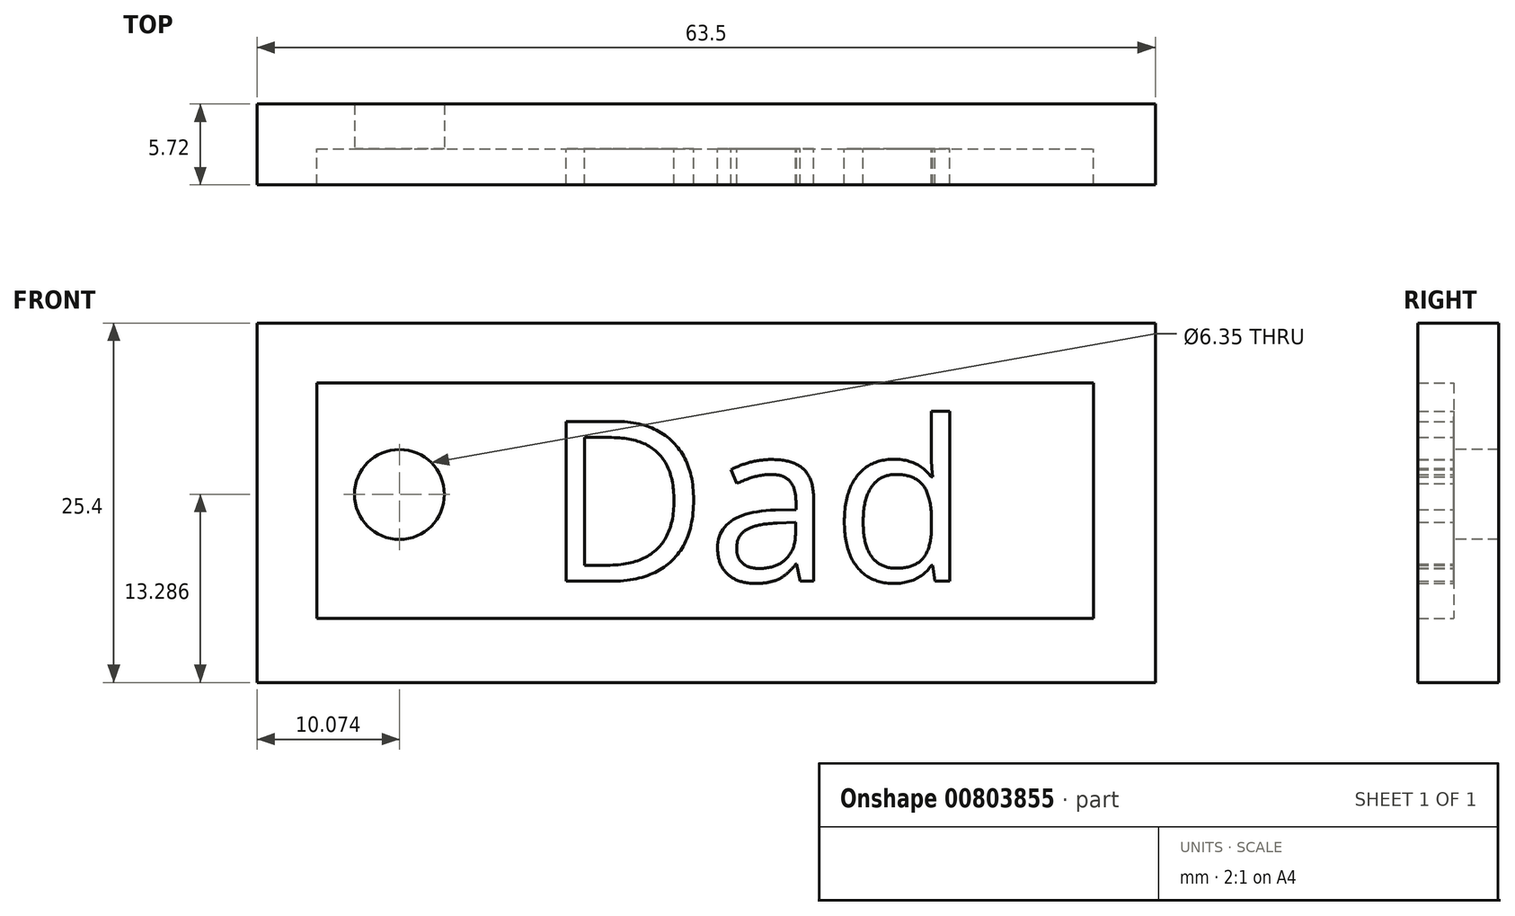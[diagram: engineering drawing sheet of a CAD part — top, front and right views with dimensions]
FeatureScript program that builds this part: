
annotation { "Feature Type Name" : "Feature", "Feature Type Description" : "" }
export const myFeature = defineFeature(function(context is Context, id is Id, definition is map)
    precondition{}
    {
        {
            var Q0;
            Q0=qCreatedBy(makeId("Front.planeOp"),FACE);
            var sketch = newSketch(context, id + "F0", { "sketchPlane" : qUnion([Q0])});
            skLineSegment(sketch, "E0.bottom", {"start": v(0, 0) * mm, "end": v(63.5, 0) * mm});
            skLineSegment(sketch, "E0.top", {"start": v(0, 25.4) * mm, "end": v(63.5, 25.4) * mm});
            skLineSegment(sketch, "E0.left", {"start": v(0, 0) * mm, "end": v(0, 25.4) * mm});
            skLineSegment(sketch, "E0.right", {"start": v(63.5, 0) * mm, "end": v(63.5, 25.4) * mm});
            skSolve(sketch);
        }
        {
            var Q0;
            Q0=makeQuery(id+"F0.imprint","IMPRINT",FACE,{"disambiguationData":[TD([[makeQuery(id+"F0.imprint","IMPRINT",EDGE,{"derivedFrom":sQuery(id+"F0.wireOp",EDGE,"E0.bottom")}),1.0]])]});
            extrude(context, id + "F1", {"entities" : qUnion([Q0]), "depth" : 3.17 * mm, "offsetDistance" : 25.4 * mm});
        }
        {
            var Q0;
            Q0=makeQuery(id+"F1.opExtrude","CAP_FACE",FACE,{"disambiguationData":[OSD([sQuery(id+"F0.wireOp",EDGE,"E0.bottom"),sQuery(id+"F0.wireOp",EDGE,"E0.top"),sQuery(id+"F0.wireOp",EDGE,"E0.left"),sQuery(id+"F0.wireOp",EDGE,"E0.right")])],"isStart":false});
            var sketch = newSketch(context, id + "F2", { "sketchPlane" : qUnion([Q0])});
            skLineSegment(sketch, "E1.bottom", {"start": v(4.23, 21.17) * mm, "end": v(59.13, 21.17) * mm});
            skLineSegment(sketch, "E1.top", {"start": v(4.23, 4.53) * mm, "end": v(59.13, 4.53) * mm});
            skLineSegment(sketch, "E1.left", {"start": v(4.23, 21.17) * mm, "end": v(4.23, 4.53) * mm});
            skLineSegment(sketch, "E1.right", {"start": v(59.13, 21.17) * mm, "end": v(59.13, 4.53) * mm});
            skSolve(sketch);
        }
        {
            var Q0;
            Q0=makeQuery(id+"F2.imprint","IMPRINT",FACE,{"disambiguationData":[TD([[makeQuery(id+"F2.imprint","IMPRINT",EDGE,{"derivedFrom":sQuery(id+"F2.wireOp",EDGE,"E1.bottom")}),1.0]])]});
            extrude(context, id + "F3", {"entities" : qUnion([Q0]), "operationType" : NewBodyOperationType.ADD, "depth" : 2.54 * mm, "offsetDistance" : 25.4 * mm});
        }
        {
            var Q0;
            Q0=makeQuery(id+"F1.opExtrude","CAP_FACE",FACE,{"disambiguationData":[OSD([sQuery(id+"F0.wireOp",EDGE,"E0.bottom"),sQuery(id+"F0.wireOp",EDGE,"E0.top"),sQuery(id+"F0.wireOp",EDGE,"E0.left"),sQuery(id+"F0.wireOp",EDGE,"E0.right")])],"isStart":false});
            var sketch = newSketch(context, id + "F4", { "sketchPlane" : qUnion([Q0])});
            skText(sketch, "E2", { "text": "Dad", "fontName": "OpenSans-Regular.ttf"});
            const initialGuessF4  = {"E2": [0.0203, 0.00715, 1, 0, 0.01139]};
            skSetInitialGuess(sketch, initialGuessF4);
            skSolve(sketch);
        }
        {
            var Q0;
            Q0 = qSketchRegion(id + "F4", true);
            extrude(context, id + "F5", {"entities" : qUnion([Q0]), "operationType" : NewBodyOperationType.ADD, "depth" : 2.54 * mm, "offsetDistance" : 25.4 * mm});
        }
        {
            var Q0;
            Q0=makeQuery(id+"F5.boolean.opBoolean","SPLIT",FACE,{"disambiguationData":[TD([makeQuery(id+"F3.opExtrude","SWEPT_FACE",FACE,{"disambiguationData":[OSD([sQuery(id+"F2.wireOp",EDGE,"E1.bottom")])]})])],"derivedFrom":makeQuery(id+"F1.opExtrude","CAP_FACE",FACE,{"disambiguationData":[OSD([sQuery(id+"F0.wireOp",EDGE,"E0.bottom"),sQuery(id+"F0.wireOp",EDGE,"E0.top"),sQuery(id+"F0.wireOp",EDGE,"E0.left"),sQuery(id+"F0.wireOp",EDGE,"E0.right")])],"isStart":false})});
            var sketch = newSketch(context, id + "F6", { "sketchPlane" : qUnion([Q0])});
            skCircle(sketch, "E3", {"center": v(10.07, 13.29) * mm, "radius": 3.93 * mm});
            skSolve(sketch);
        }
        {
            var Q0;
            Q0=sQuery(id+"F6.wireOp",VERTEX,"E3.center");
            var Q1;
            Q1=makeQuery(id+"F1.opExtrude","SWEPT_BODY",BODY,{"disambiguationData":[OSD([sQuery(id+"F0.wireOp",EDGE,"E0.bottom"),sQuery(id+"F0.wireOp",EDGE,"E0.top"),sQuery(id+"F0.wireOp",EDGE,"E0.left"),sQuery(id+"F0.wireOp",EDGE,"E0.right")])]});
            hole(context, id + "F7", {"style" : HoleStyle.SIMPLE, "endStyle" : HoleEndStyle.THROUGH, "holeDiameter" : 6.35 * mm, "majorDiameter" : 6.35 * mm, "isTappedThrough" : true, "tappedDepth" : 12.7 * mm, "tapClearance" : 3, "locations" : qUnion([Q0]), "scope" : qUnion([Q1])});
        }
    });
